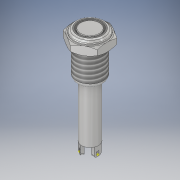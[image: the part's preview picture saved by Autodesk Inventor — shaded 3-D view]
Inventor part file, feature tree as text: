
AUTODESK INVENTOR PART (.ipt)
format: ipt  version: 2019.4 (Build 234330000, 330)  size: 296,960 bytes
history: native  units: mm
features: extrude x9, sketch x6, fillet x4, chamfer x3, revolve x1, boolean_combine x1, plane x1, other x1, pattern_circular x1, thread x1
ambient origin geometry x8: Origin, YZ Plane, XZ Plane, XY Plane, X Axis, Y Axis, Z Axis, Center Point
bodies: Solid1 (feature_tree), Solid2 (feature_tree)
feature tree (28):
  sketch  "Sketch1"  dims[d0=13.0mm d1=14.0mm]
  extrude  "Extrusion1"  Depth=14.0mm
  extrude  "Extrusion2"  Depth=18.0mm TaperAngle=0.0deg
  extrude  "Extrusion3"  Depth=5.0mm TaperAngle=0.0deg
  extrude  "Extrusion4"  Depth=1.0mm TaperAngle=45.0deg
  sketch  "Sketch3"  dims[d5=5.0mm d6=0.0mm d7=5.0mm d8=0.0mm]
  chamfer  "Chamfer1"  Distance=8.0mm
  fillet  "Fillet1"  Radius=1.0mm
  fillet  "Fillet2"  Radius=0.5mm
  sketch  "Sketch2"  dims[d2=11.0mm d3=18.0mm d4=0.0mm]
  extrude  "Extrusion5"  Depth=1.0mm TaperAngle=0.0deg
  chamfer  "Chamfer2"  Distance=0.2mm
  extrude  "Extrusion6"  Depth=3.5mm
  fillet  "Fillet3"  Radius=1.0mm
  revolve  "Revolution1"  [1 undecoded]
  boolean_combine  "Combine1"
  extrude  "Extrusion10"  Depth=2.0mm
  plane  "Work Plane1"
  extrude  "Extrusion7"  TaperAngle=90.0deg  [1 undecoded]
  fillet  "Fillet4"  Radius=1.0mm
  extrude  "Extrusion8"  Depth=2.0mm
  other  "Work Axis1"
  pattern_circular  "Circular Pattern1"  Count=3 Angle=360.0deg
  thread  "Thread1"  [1 undecoded]
  chamfer  "Chamfer3"  Distance=1.0mm
  sketch  "Sketch4"  dims[d9=1.5mm d10=0.0mm d11=1.0mm d12=2.0mm d13=45.0deg]
  sketch  "Sketch5"  dims[d14=1.0mm]
  sketch  "Sketch7"  dims[d15=2.0mm d16=8.0mm d17=1.0mm d18=0.0mm d19=0.5mm d20=2.0mm d21=45.0deg d22=1.0mm d23=0.0mm d24=0.2mm d25=3.5mm d26=1.0mm d27=6.108652mm d28=6.108652mm d29=90.0deg d31=1.0mm d32=3.0mm d33=30.0mm d35=360.0deg d37=1.0mm d38=0.0mm d39=1.0mm d40=1.2mm d41=1.0mm d42=0.0mm d43=30.0mm d44=360.0deg d46=10.0mm d47=0.0mm d48=0.2mm d49=2.0mm d50=45.0deg d53=22.0mm d54=0.0mm d55=4.0mm]
note: 3 required parameter values undecoded (feature->parameter linkage not recoverable at this tier; creation-order binding heuristic only, values carry confidence <= 0.55)